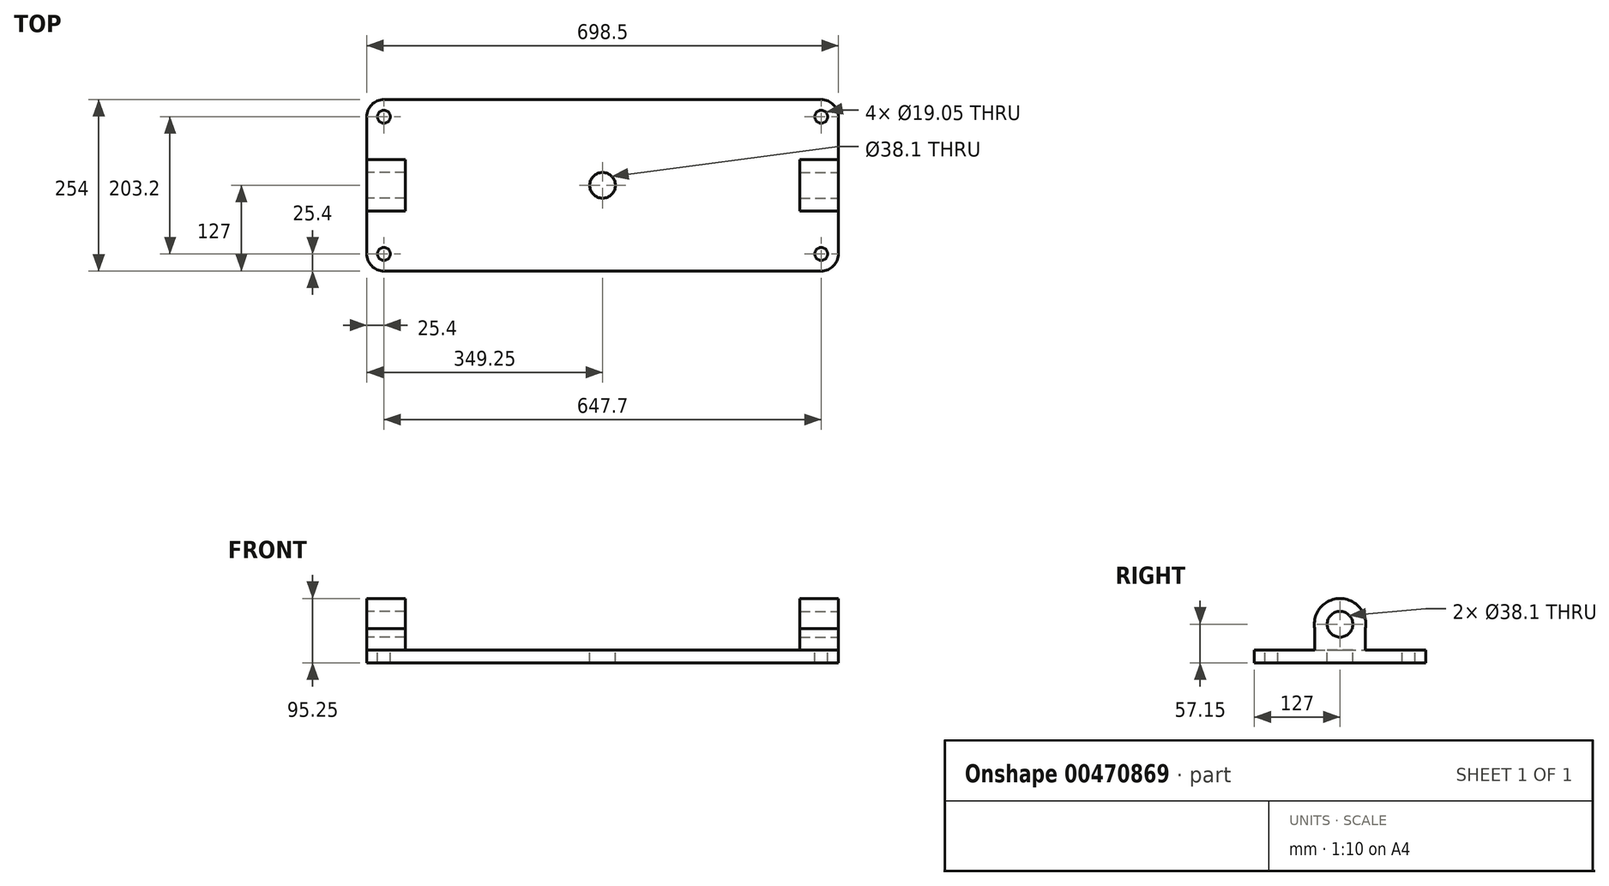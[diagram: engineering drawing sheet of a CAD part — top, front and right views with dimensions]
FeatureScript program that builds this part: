
annotation { "Feature Type Name" : "Feature", "Feature Type Description" : "" }
export const myFeature = defineFeature(function(context is Context, id is Id, definition is map)
    precondition{}
    {
        {
            var Q0;
            Q0=qCreatedBy(makeId("Top.planeOp"),FACE);
            var sketch = newSketch(context, id + "F0", { "sketchPlane" : qUnion([Q0])});
            skCircle(sketch, "E0", {"center": v(0, 0) * mm, "radius": 19.05 * mm});
            skLineSegment(sketch, "E1", {"start": v(0, 0) * mm, "end": v(349.25, 0) * mm});
            skLineSegment(sketch, "E2", {"start": v(349.25, 0) * mm, "end": v(349.25, 101.6) * mm});
            skLineSegment(sketch, "E3", {"start": v(323.85, 127) * mm, "end": v(-323.85, 127) * mm});
            skLineSegment(sketch, "E4", {"start": v(-349.25, 101.6) * mm, "end": v(-349.25, -101.6) * mm});
            skLineSegment(sketch, "E5", {"start": v(-323.85, -127) * mm, "end": v(323.85, -127) * mm});
            skLineSegment(sketch, "E6", {"start": v(349.25, -101.6) * mm, "end": v(349.25, 0) * mm});
            skPoint(sketch, "E7.visualSharp", {"position": v(-349.25, 127) * mm});
            skArc(sketch, "E7.filletArc", {"start": v(-323.85, 127) * mm, "mid": v(-341.81, 119.56) * mm, "end": v(-349.25, 101.6) * mm});
            skPoint(sketch, "E8.visualSharp", {"position": v(-349.25, -127) * mm});
            skArc(sketch, "E8.filletArc", {"start": v(-349.25, -101.6) * mm, "mid": v(-341.81, -119.56) * mm, "end": v(-323.85, -127) * mm});
            skPoint(sketch, "E9.visualSharp", {"position": v(349.25, -127) * mm});
            skArc(sketch, "E9.filletArc", {"start": v(323.85, -127) * mm, "mid": v(341.81, -119.56) * mm, "end": v(349.25, -101.6) * mm});
            skPoint(sketch, "E10.visualSharp", {"position": v(349.25, 127) * mm});
            skArc(sketch, "E10.filletArc", {"start": v(349.25, 101.6) * mm, "mid": v(341.81, 119.56) * mm, "end": v(323.85, 127) * mm});
            skCircle(sketch, "E11", {"center": v(323.85, -101.6) * mm, "radius": 9.53 * mm});
            skCircle(sketch, "E12.MirrorC", {"center": v(323.85, 101.6) * mm, "radius": 9.53 * mm});
            skLineSegment(sketch, "E13", {"start": v(0, 0) * mm, "end": v(0, 127) * mm});
            skCircle(sketch, "E14.MirrorC", {"center": v(-323.85, 101.6) * mm, "radius": 9.53 * mm});
            skCircle(sketch, "E15.MirrorC", {"center": v(-323.85, -101.6) * mm, "radius": 9.53 * mm});
            skSolve(sketch);
        }
        {
            var Q0;
            Q0=makeQuery(id+"F0.imprint","IMPRINT",FACE,{"disambiguationData":[TD([[makeQuery(id+"F0.imprint","IMPRINT",EDGE,{"derivedFrom":sQuery(id+"F0.wireOp",EDGE,"E4")}),1.0]])]});
            var Q1;
            {var subQ0=sQuery(id+"F0.wireOp",EDGE,"E2");Q1=makeQuery(id+"F0.imprint","IMPRINT",FACE,{"disambiguationData":[TD([[makeQuery(id+"F0.imprint","IMPRINT",EDGE,{"derivedFrom":subQ0}),1.0]])]});}
            extrude(context, id + "F1", {"entities" : qUnion([Q0, Q1]), "oppositeDirection" : true, "depth" : 19.05 * mm});
        }
        {
            var Q0;
            Q0=makeQuery(id+"F1.opExtrude","SWEPT_FACE",FACE,{"disambiguationData":[OSD([sQuery(id+"F0.wireOp",EDGE,"E4")])]});
            var sketch = newSketch(context, id + "F2", { "sketchPlane" : qUnion([Q0])});
            skLineSegment(sketch, "E16", {"start": v(0, -19.05) * mm, "end": v(0, 38.1) * mm});
            skCircle(sketch, "E17", {"center": v(0, 38.1) * mm, "radius": 19.05 * mm});
            skCircle(sketch, "E18", {"center": v(0, 38.1) * mm, "radius": 38.1 * mm});
            skLineSegment(sketch, "E19", {"start": v(-37.57, 31.75) * mm, "end": v(-37.57, 0) * mm});
            skLineSegment(sketch, "E20.MirrorCS", {"start": v(37.57, 31.75) * mm, "end": v(37.57, 0) * mm});
            skSolve(sketch);
        }
        {
            var Q0;
            Q0=makeQuery(id+"F2.imprint","IMPRINT",FACE,{"disambiguationData":[TD([[makeQuery(id+"F2.imprint","IMPRINT",EDGE,{"derivedFrom":sQuery(id+"F2.wireOp",EDGE,"E17")}),-1.0]])]});
            var Q1;
            {var subQ0=sQuery(id+"F2.wireOp",EDGE,"E19");Q1=makeQuery(id+"F2.imprint","IMPRINT",FACE,{"disambiguationData":[TD([[makeQuery(id+"F2.imprint","IMPRINT",EDGE,{"derivedFrom":subQ0}),1.0]])]});}
            var Q2;
            {var subQ0=sQuery(id+"F2.wireOp",EDGE,"E20.MirrorCS");Q2=makeQuery(id+"F2.imprint","IMPRINT",FACE,{"disambiguationData":[TD([[makeQuery(id+"F2.imprint","IMPRINT",EDGE,{"derivedFrom":subQ0}),-1.0]])]});}
            extrude(context, id + "F3", {"entities" : qUnion([Q0, Q1, Q2]), "operationType" : NewBodyOperationType.ADD, "oppositeDirection" : true, "depth" : 57.15 * mm});
        }
        {
            var Q0;
            Q0=makeQuery(id+"F1.opExtrude","SWEPT_FACE",FACE,{"disambiguationData":[OSD([sQuery(id+"F0.wireOp",EDGE,"E2"),sQuery(id+"F0.wireOp",EDGE,"E6")])]});
            var sketch = newSketch(context, id + "F4", { "sketchPlane" : qUnion([Q0])});
            skLineSegment(sketch, "E21", {"start": v(0, -19.05) * mm, "end": v(0, 38.1) * mm});
            skCircle(sketch, "E22", {"center": v(0, 38.1) * mm, "radius": 19.05 * mm});
            skCircle(sketch, "E23", {"center": v(0, 38.1) * mm, "radius": 38.1 * mm});
            skLineSegment(sketch, "E24", {"start": v(-37.57, 31.75) * mm, "end": v(-37.57, 0) * mm});
            skLineSegment(sketch, "E25.MirrorCS", {"start": v(37.57, 31.75) * mm, "end": v(37.57, 0) * mm});
            skSolve(sketch);
        }
        {
            var Q0;
            {var subQ0=sQuery(id+"F4.wireOp",EDGE,"E25.MirrorCS");Q0=makeQuery(id+"F4.imprint","IMPRINT",FACE,{"disambiguationData":[TD([[makeQuery(id+"F4.imprint","IMPRINT",EDGE,{"derivedFrom":subQ0}),-1.0]])]});}
            var Q1;
            Q1=makeQuery(id+"F4.imprint","IMPRINT",FACE,{"disambiguationData":[TD([[makeQuery(id+"F4.imprint","IMPRINT",EDGE,{"derivedFrom":sQuery(id+"F4.wireOp",EDGE,"E22")}),-1.0]])]});
            var Q2;
            {var subQ0=sQuery(id+"F4.wireOp",EDGE,"E24");Q2=makeQuery(id+"F4.imprint","IMPRINT",FACE,{"disambiguationData":[TD([[makeQuery(id+"F4.imprint","IMPRINT",EDGE,{"derivedFrom":subQ0}),1.0]])]});}
            extrude(context, id + "F5", {"entities" : qUnion([Q0, Q1, Q2]), "operationType" : NewBodyOperationType.ADD, "oppositeDirection" : true, "depth" : 57.15 * mm});
        }
    });
